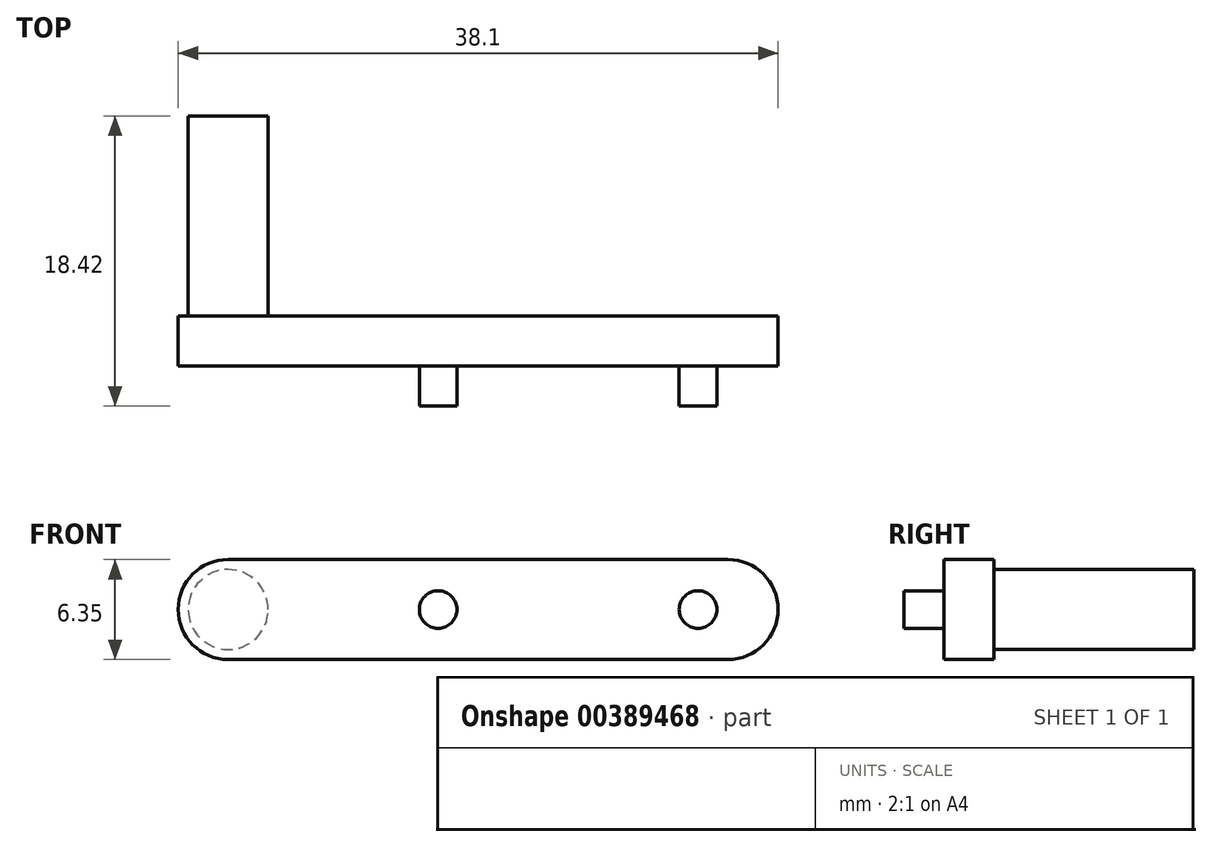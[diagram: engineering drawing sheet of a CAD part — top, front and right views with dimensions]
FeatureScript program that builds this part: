
annotation { "Feature Type Name" : "Feature", "Feature Type Description" : "" }
export const myFeature = defineFeature(function(context is Context, id is Id, definition is map)
    precondition{}
    {
        {
            var Q0;
            Q0=qCreatedBy(makeId("Front.planeOp"),FACE);
            var sketch = newSketch(context, id + "F0", { "sketchPlane" : qUnion([Q0])});
            skLineSegment(sketch, "E0.bottom", {"start": v(-5.23, 6.35) * mm, "end": v(26.52, 6.35) * mm});
            skLineSegment(sketch, "E0.top", {"start": v(-5.23, 0) * mm, "end": v(26.52, 0) * mm});
            skLineSegment(sketch, "E0.left", {"start": v(-8.4, 3.18) * mm, "end": v(-8.4, 3.18) * mm});
            skLineSegment(sketch, "E0.right", {"start": v(29.7, 3.18) * mm, "end": v(29.7, 3.18) * mm});
            skPoint(sketch, "E1.visualSharp", {"position": v(-8.4, 6.35) * mm});
            skArc(sketch, "E1.filletArc", {"start": v(-5.23, 6.35) * mm, "mid": v(-7.47, 5.42) * mm, "end": v(-8.4, 3.17) * mm});
            skPoint(sketch, "E2.visualSharp", {"position": v(29.7, 6.35) * mm});
            skArc(sketch, "E2.filletArc", {"start": v(29.7, 3.17) * mm, "mid": v(28.77, 5.42) * mm, "end": v(26.52, 6.35) * mm});
            skPoint(sketch, "E3.visualSharp", {"position": v(29.7, 0) * mm});
            skArc(sketch, "E3.filletArc", {"start": v(26.52, 0) * mm, "mid": v(28.77, 0.93) * mm, "end": v(29.7, 3.18) * mm});
            skPoint(sketch, "E4.visualSharp", {"position": v(-8.4, 0) * mm});
            skArc(sketch, "E4.filletArc", {"start": v(-8.4, 3.17) * mm, "mid": v(-7.47, 0.93) * mm, "end": v(-5.23, 0) * mm});
            skSolve(sketch);
        }
        {
            var Q0;
            Q0=makeQuery(id+"F0.imprint","IMPRINT",FACE,{"disambiguationData":[TD([[makeQuery(id+"F0.imprint","IMPRINT",EDGE,{"derivedFrom":sQuery(id+"F0.wireOp",EDGE,"E0.bottom")}),-1.0]])]});
            extrude(context, id + "F1", {"entities" : qUnion([Q0]), "depth" : 3.17 * mm});
        }
        {
            var Q0;
            Q0=makeQuery(id+"F1.opExtrude","CAP_FACE",FACE,{"disambiguationData":[OSD([sQuery(id+"F0.wireOp",EDGE,"E0.bottom"),sQuery(id+"F0.wireOp",EDGE,"E0.top"),sQuery(id+"F0.wireOp",EDGE,"E1.filletArc"),sQuery(id+"F0.wireOp",EDGE,"E2.filletArc"),sQuery(id+"F0.wireOp",EDGE,"E3.filletArc"),sQuery(id+"F0.wireOp",EDGE,"E4.filletArc")])],"isStart":true});
            var sketch = newSketch(context, id + "F2", { "sketchPlane" : qUnion([Q0])});
            skCircle(sketch, "E5", {"center": v(5.23, 3.17) * mm, "radius": 2.54 * mm});
            skSolve(sketch);
        }
        {
            var Q0;
            Q0 = qSketchRegion(id + "F2", true);
            extrude(context, id + "F3", {"entities" : qUnion([Q0]), "operationType" : NewBodyOperationType.ADD, "depth" : 12.7 * mm});
        }
        {
            var Q0;
            Q0=makeQuery(id+"F1.opExtrude","CAP_FACE",FACE,{"disambiguationData":[OSD([sQuery(id+"F0.wireOp",EDGE,"E0.bottom"),sQuery(id+"F0.wireOp",EDGE,"E0.top"),sQuery(id+"F0.wireOp",EDGE,"E1.filletArc"),sQuery(id+"F0.wireOp",EDGE,"E2.filletArc"),sQuery(id+"F0.wireOp",EDGE,"E3.filletArc"),sQuery(id+"F0.wireOp",EDGE,"E4.filletArc")])],"isStart":false});
            var sketch = newSketch(context, id + "F4", { "sketchPlane" : qUnion([Q0])});
            skCircle(sketch, "E6", {"center": v(8.1, 3.18) * mm, "radius": 1.2 * mm});
            skCircle(sketch, "E7", {"center": v(24.62, 3.17) * mm, "radius": 1.2 * mm});
            skPoint(sketch, "E8", {"position": v(-8.4, 3.17) * mm});
            skPoint(sketch, "E9", {"position": v(29.7, 3.18) * mm});
            skSolve(sketch);
        }
        {
            var Q0;
            Q0 = qSketchRegion(id + "F4", true);
            extrude(context, id + "F5", {"entities" : qUnion([Q0]), "operationType" : NewBodyOperationType.ADD, "depth" : 2.54 * mm});
        }
    });
